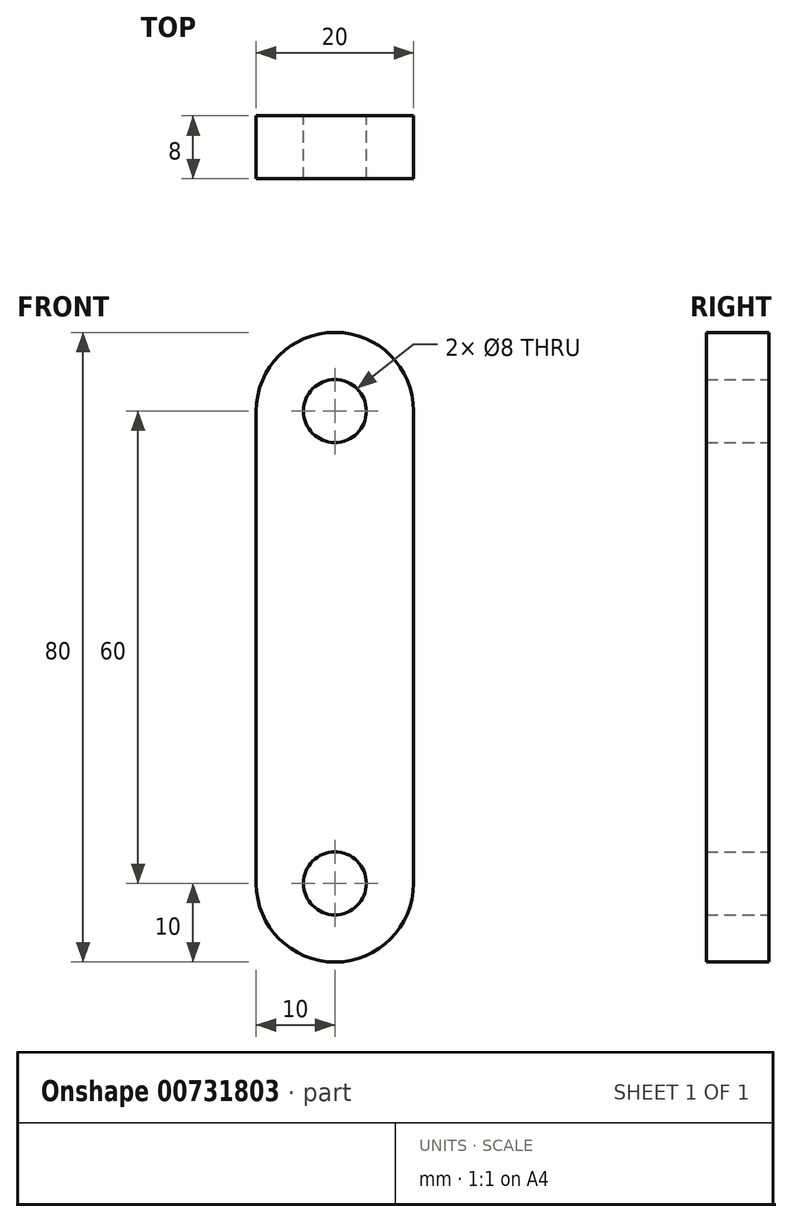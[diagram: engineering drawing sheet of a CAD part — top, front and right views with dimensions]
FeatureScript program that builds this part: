
annotation { "Feature Type Name" : "Feature", "Feature Type Description" : "" }
export const myFeature = defineFeature(function(context is Context, id is Id, definition is map)
    precondition{}
    {
        {
            var Q0;
            Q0=qCreatedBy(makeId("Front.planeOp"),FACE);
            var sketch = newSketch(context, id + "F0", { "sketchPlane" : qUnion([Q0])});
            skCircle(sketch, "E0", {"center": v(0, 0) * mm, "radius": 4 * mm});
            skArc(sketch, "E1", {"start": v(-10, 0) * mm, "mid": v(0, -10) * mm, "end": v(10, 0) * mm});
            skLineSegment(sketch, "E2", {"start": v(-10, 0) * mm, "end": v(-10, 60) * mm});
            skLineSegment(sketch, "E3", {"start": v(10, 0) * mm, "end": v(10, 60) * mm});
            skArc(sketch, "E4", {"start": v(10, 60) * mm, "mid": v(0, 70) * mm, "end": v(-10, 60) * mm});
            skCircle(sketch, "E5", {"center": v(0, 60) * mm, "radius": 4 * mm});
            skSolve(sketch);
        }
        {
            var Q0;
            Q0 = qSketchRegion(id + "F0", true);
            extrude(context, id + "F1", {"entities" : qUnion([Q0]), "depth" : 8 * mm, "offsetDistance" : 25 * mm});
        }
    });
